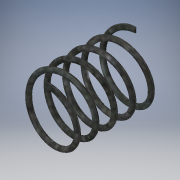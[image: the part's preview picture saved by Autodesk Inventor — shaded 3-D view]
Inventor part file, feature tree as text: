
AUTODESK INVENTOR PART (.ipt)
format: ipt  version: 2019 (Build 230136000, 136)  size: 274,432 bytes
history: native  units: mm
features: sketch x2, other x1, extrude x1, projected_geometry x1
ambient origin geometry x8: Origin, YZ Plane, XZ Plane, XY Plane, X Axis, Y Axis, Z Axis, Center Point
bodies: Solide1 (feature_tree)
feature tree (5):
  other  "Hélicoïde1"
  extrude  "Extrusion1"  Depth=1.5mm
  sketch  "Esquisse1"
  sketch  "Esquisse2"
  projected_geometry  "Boucle projetée1"
